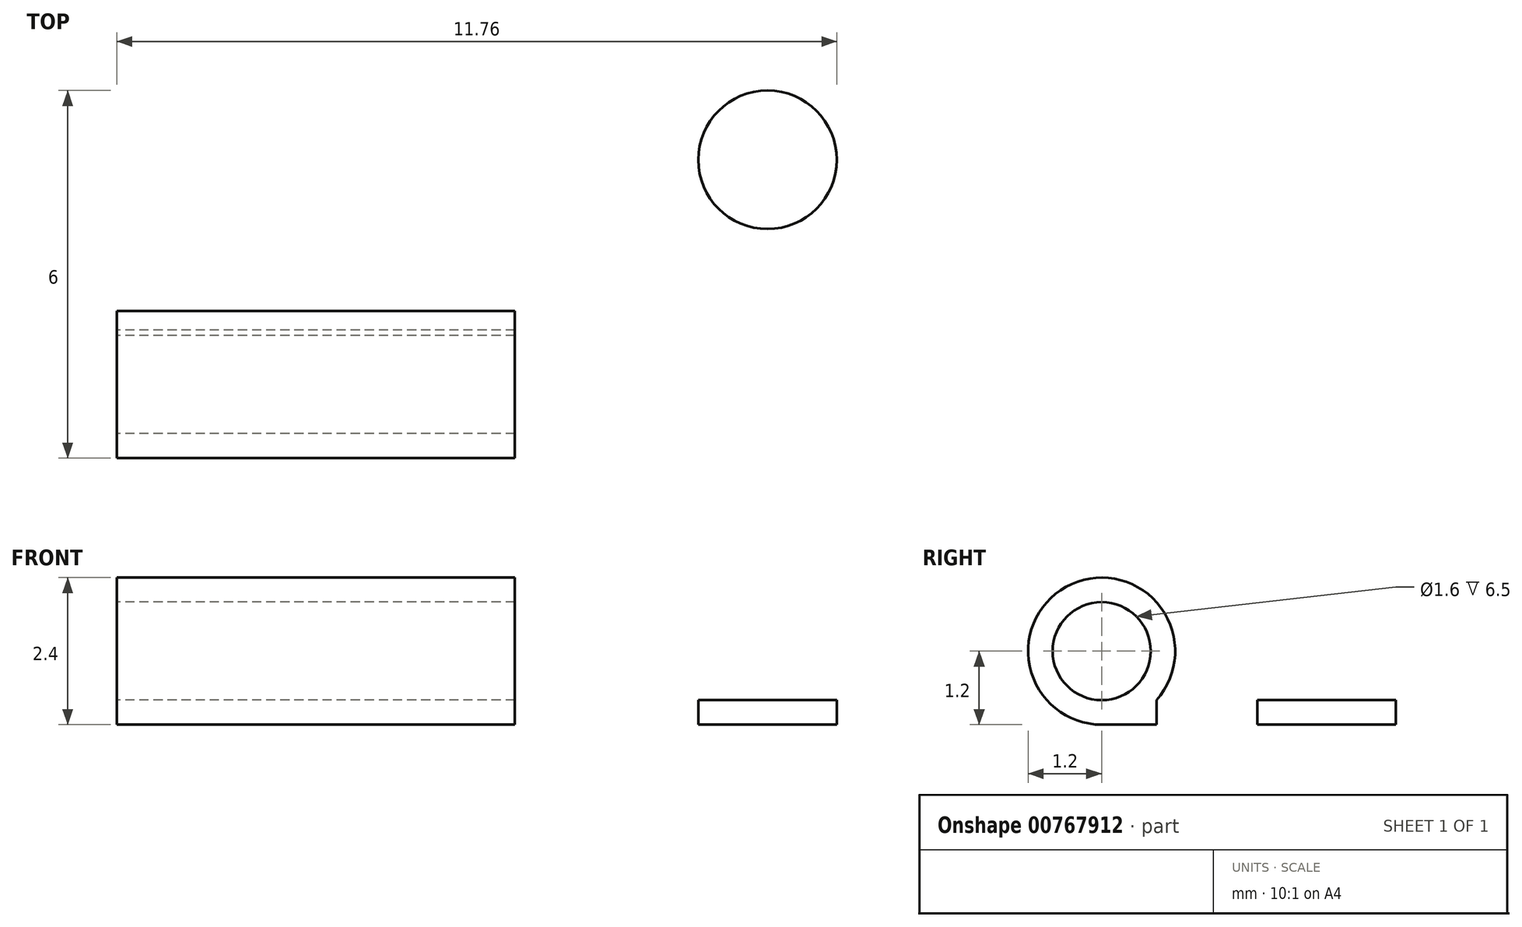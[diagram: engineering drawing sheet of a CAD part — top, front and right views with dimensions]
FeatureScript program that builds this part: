
annotation { "Feature Type Name" : "Feature", "Feature Type Description" : "" }
export const myFeature = defineFeature(function(context is Context, id is Id, definition is map)
    precondition{}
    {
        {
            var Q0;
            Q0=qCreatedBy(makeId("Right.planeOp"),FACE);
            var sketch = newSketch(context, id + "F0", { "sketchPlane" : qUnion([Q0])});
            skLineSegment(sketch, "E0", {"start": v(0, 0) * mm, "end": v(6.1, 0) * mm});
            skArc(sketch, "E1", {"start": v(0, 2.4) * mm, "mid": v(-1.2, 1.2) * mm, "end": v(0, 0) * mm});
            skLineSegment(sketch, "E2.0", {"start": v(0.9, 0.4) * mm, "end": v(6.1, 0.4) * mm});
            skArc(sketch, "E3", {"start": v(0, 2.4) * mm, "mid": v(1.1, 1.69) * mm, "end": v(0.9, 0.4) * mm});
            skLineSegment(sketch, "E4", {"start": v(6.1, 0) * mm, "end": v(6.1, 0.4) * mm});
            skCircle(sketch, "E5", {"center": v(0, 1.2) * mm, "radius": 0.8 * mm});
            skSolve(sketch);
        }
        {
            var Q0;
            Q0=makeQuery(id+"F0.imprint","IMPRINT",FACE,{"disambiguationData":[TD([[makeQuery(id+"F0.imprint","IMPRINT",EDGE,{"derivedFrom":sQuery(id+"F0.wireOp",EDGE,"E0")}),1.0]])]});
            extrude(context, id + "F1", {"entities" : qUnion([Q0]), "depth" : 13 * mm, "offsetDistance" : 25 * mm});
        }
        {
            var Q0;
            Q0=makeQuery(id+"F1.opExtrude","CAP_FACE",FACE,{"disambiguationData":[OSD([sQuery(id+"F0.wireOp",EDGE,"E0"),sQuery(id+"F0.wireOp",EDGE,"E1"),sQuery(id+"F0.wireOp",EDGE,"E2.0"),sQuery(id+"F0.wireOp",EDGE,"E3"),sQuery(id+"F0.wireOp",EDGE,"E4"),sQuery(id+"F0.wireOp",EDGE,"E5")])],"isStart":false});
            var sketch = newSketch(context, id + "F2", { "sketchPlane" : qUnion([Q0])});
            skLineSegment(sketch, "E6", {"start": v(0.9, 0.4) * mm, "end": v(0.9, 0) * mm});
            skSolve(sketch);
        }
        {
            var Q0;
            {var subQ0=sQuery(id+"F2.wireOp",EDGE,"E6");Q0=makeQuery(id+"F2.imprint","IMPRINT",FACE,{"disambiguationData":[TD([[makeQuery(id+"F2.imprint","IMPRINT",EDGE,{"derivedFrom":subQ0}),-1.0]])]});}
            extrude(context, id + "F3", {"entities" : qUnion([Q0]), "operationType" : NewBodyOperationType.REMOVE, "oppositeDirection" : true, "depth" : (13 / 2) * mm, "offsetDistance" : 25 * mm});
        }
        {
            var Q0;
            Q0=makeQuery(id+"F1.opExtrude","SWEPT_FACE",FACE,{"disambiguationData":[OSD([sQuery(id+"F0.wireOp",EDGE,"E2.0")])]});
            var sketch = newSketch(context, id + "F4", { "sketchPlane" : qUnion([Q0])});
            skCircle(sketch, "E7", {"center": v(2.38, 3.67) * mm, "radius": 1.13 * mm});
            skLineSegment(sketch, "E8", {"start": v(0, 4.8) * mm, "end": v(13, 4.8) * mm, "construction": true});
            skLineSegment(sketch, "E9", {"start": v(6.5, 4.8) * mm, "end": v(6.5, 2.56) * mm, "construction": true});
            skCircle(sketch, "E10.MirrorC", {"center": v(10.62, 3.67) * mm, "radius": 1.13 * mm});
            skSolve(sketch);
        }
        {
            var Q0;
            Q0=makeQuery(id+"F4.imprint","IMPRINT",FACE,{"disambiguationData":[TD([[makeQuery(id+"F4.imprint","IMPRINT",EDGE,{"derivedFrom":sQuery(id+"F4.wireOp",EDGE,"E7")}),1.0]])]});
            var Q1;
            Q1=makeQuery(id+"F4.imprint","IMPRINT",FACE,{"disambiguationData":[TD([[makeQuery(id+"F4.imprint","IMPRINT",EDGE,{"derivedFrom":sQuery(id+"F4.wireOp",EDGE,"E10.MirrorC")}),-1.0]])]});
            extrude(context, id + "F5", {"entities" : qUnion([Q0, Q1]), "operationType" : NewBodyOperationType.REMOVE, "endBound" : BoundingType.UP_TO_NEXT, "oppositeDirection" : true, "depth" : 25 * mm, "offsetDistance" : 25 * mm});
        }
    });
